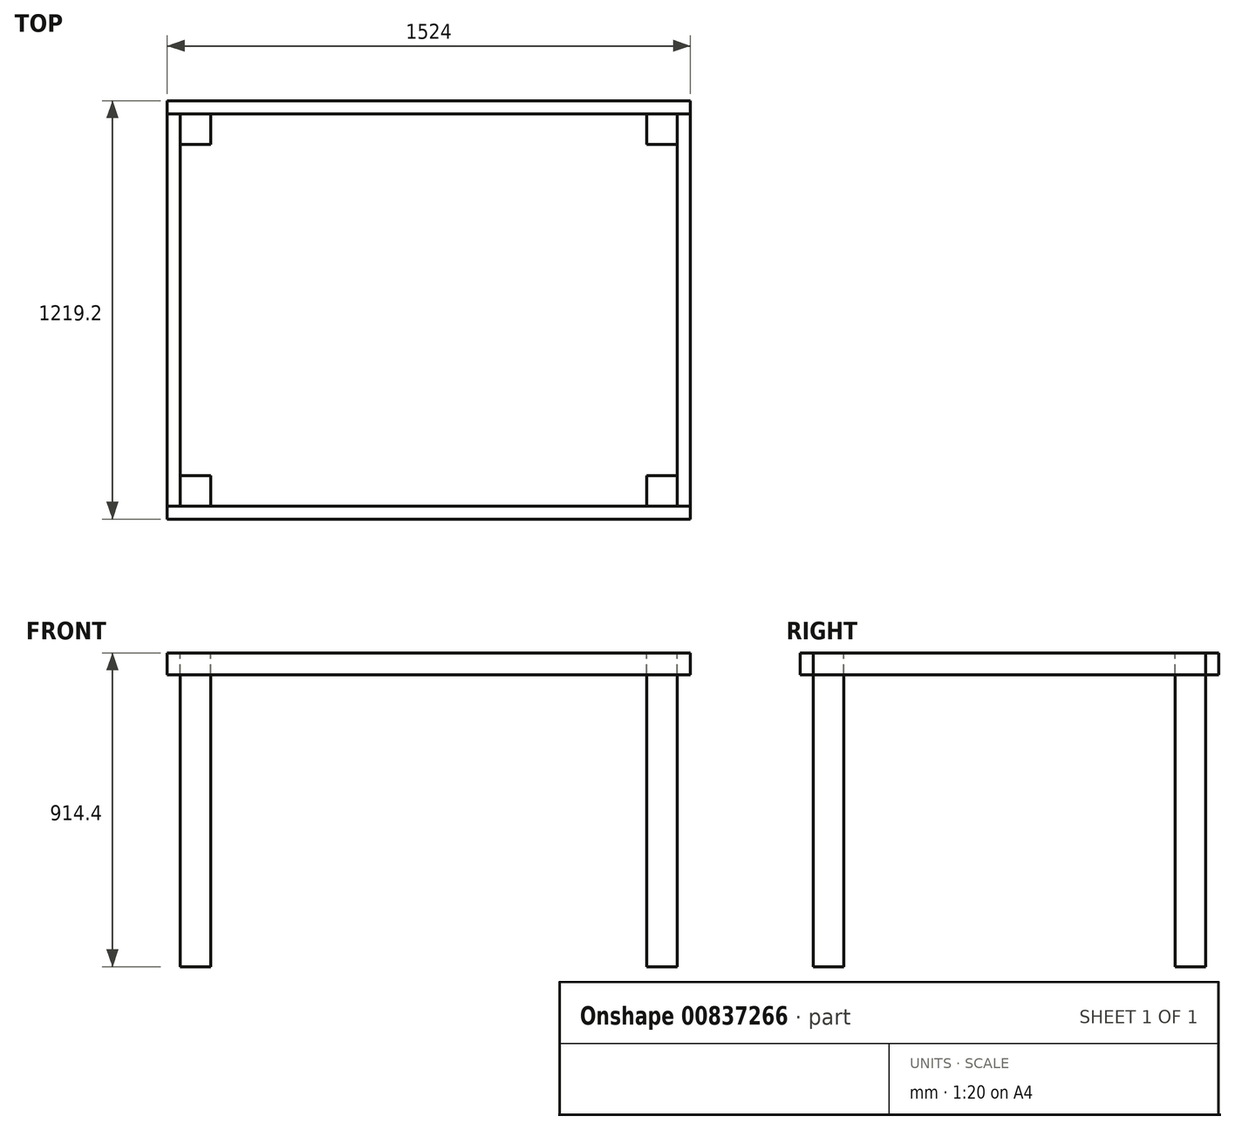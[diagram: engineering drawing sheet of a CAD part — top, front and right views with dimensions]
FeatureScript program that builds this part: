
annotation { "Feature Type Name" : "Feature", "Feature Type Description" : "" }
export const myFeature = defineFeature(function(context is Context, id is Id, definition is map)
    precondition{}
    {
        {
            var Q0;
            Q0=qCreatedBy(makeId("Top.planeOp"),FACE);
            var sketch = newSketch(context, id + "F0", { "sketchPlane" : qUnion([Q0])});
            skLineSegment(sketch, "E0.bottom", {"start": v(-762, -609.6) * mm, "end": v(762, -609.6) * mm});
            skLineSegment(sketch, "E0.top", {"start": v(-762, 609.6) * mm, "end": v(762, 609.6) * mm});
            skLineSegment(sketch, "E0.left", {"start": v(-762, -609.6) * mm, "end": v(-762, 609.6) * mm});
            skLineSegment(sketch, "E0.right", {"start": v(762, -609.6) * mm, "end": v(762, 609.6) * mm});
            skLineSegment(sketch, "E1", {"start": v(-762, -571.5) * mm, "end": v(762, -571.5) * mm});
            skLineSegment(sketch, "E2.MirrorCS", {"start": v(-762, 571.5) * mm, "end": v(762, 571.5) * mm});
            skLineSegment(sketch, "E3", {"start": v(-723.9, 571.5) * mm, "end": v(-723.9, -571.5) * mm});
            skLineSegment(sketch, "E4.MirrorCS", {"start": v(723.9, 571.5) * mm, "end": v(723.9, -571.5) * mm});
            skPoint(sketch, "E5.orphan", {"position": v(-723.9, -571.5) * mm});
            skPoint(sketch, "E6.orphan", {"position": v(-723.9, 571.5) * mm});
            skPoint(sketch, "E7.orphan", {"position": v(723.9, 571.5) * mm});
            skPoint(sketch, "E8.orphan", {"position": v(723.9, -571.5) * mm});
            skLineSegment(sketch, "E9.bottom", {"start": v(-723.9, -571.5) * mm, "end": v(-635, -571.5) * mm});
            skLineSegment(sketch, "E9.top", {"start": v(-723.9, -482.6) * mm, "end": v(-635, -482.6) * mm});
            skLineSegment(sketch, "E9.left", {"start": v(-723.9, -571.5) * mm, "end": v(-723.9, -482.6) * mm});
            skLineSegment(sketch, "E9.right", {"start": v(-635, -571.5) * mm, "end": v(-635, -482.6) * mm});
            skLineSegment(sketch, "E10.MirrorCS", {"start": v(-723.9, 482.6) * mm, "end": v(-635, 482.6) * mm});
            skLineSegment(sketch, "E11.MirrorCS", {"start": v(-635, 571.5) * mm, "end": v(-635, 482.6) * mm});
            skLineSegment(sketch, "E12.MirrorCS", {"start": v(635, 571.5) * mm, "end": v(635, 482.6) * mm});
            skLineSegment(sketch, "E13.MirrorCS", {"start": v(723.9, 482.6) * mm, "end": v(635, 482.6) * mm});
            skLineSegment(sketch, "E14.MirrorCS", {"start": v(723.9, -482.6) * mm, "end": v(635, -482.6) * mm});
            skLineSegment(sketch, "E15.MirrorCS", {"start": v(635, -571.5) * mm, "end": v(635, -482.6) * mm});
            skLineSegment(sketch, "E16", {"start": v(0, 127) * mm, "end": v(0, -127) * mm});
            skLineSegment(sketch, "E17", {"start": v(-127, 0) * mm, "end": v(127, 0) * mm});
            skLineSegment(sketch, "E18.MirrorCS", {"start": v(-635, 533.4) * mm, "end": v(635, 533.4) * mm});
            skLineSegment(sketch, "E19.MirrorCS", {"start": v(-635, -533.4) * mm, "end": v(635, -533.4) * mm});
            skLineSegment(sketch, "E20.MirrorCS", {"start": v(-685.8, -482.6) * mm, "end": v(-685.8, 482.6) * mm});
            skPoint(sketch, "E21.orphan", {"position": v(-762, -533.4) * mm});
            skPoint(sketch, "E22.orphan", {"position": v(-762, 533.4) * mm});
            skPoint(sketch, "E23.orphan", {"position": v(762, 533.4) * mm});
            skPoint(sketch, "E24.orphan", {"position": v(762, -533.4) * mm});
            skPoint(sketch, "E25.orphan", {"position": v(685.8, -609.6) * mm});
            skLineSegment(sketch, "E26.trimOffspring", {"start": v(685.8, -482.6) * mm, "end": v(685.8, 482.6) * mm});
            skPoint(sketch, "E27.orphan", {"position": v(-685.8, -609.6) * mm});
            skPoint(sketch, "E28.trimOffspring.end.orphan", {"position": v(-685.8, 609.6) * mm});
            skPoint(sketch, "E29.orphan", {"position": v(685.8, 609.6) * mm});
            skSolve(sketch);
        }
        {
            var Q0;
            {var subQ0=sQuery(id+"F0.wireOp",EDGE,"E9.top");Q0=makeQuery(id+"F0.imprint","IMPRINT",FACE,{"disambiguationData":[TD([[makeQuery(id+"F0.imprint","IMPRINT",EDGE,{"derivedFrom":subQ0}),-1.0]])]});}
            var Q1;
            {var subQ0=sQuery(id+"F0.wireOp",EDGE,"E9.bottom");Q1=makeQuery(id+"F0.imprint","IMPRINT",FACE,{"disambiguationData":[TD([[makeQuery(id+"F0.imprint","IMPRINT",EDGE,{"derivedFrom":subQ0}),1.0]])]});}
            extrude(context, id + "F1", {"entities" : qUnion([Q0, Q1]), "depth" : -914.4 * mm, "offsetDistance" : 25.4 * mm});
        }
        {
            var Q0;
            {var subQ0=sQuery(id+"F0.wireOp",EDGE,"E0.left");var subQ1=sQuery(id+"F0.wireOp",EDGE,"E0.bottom");var subQ2=makeQuery(id+"F0.imprint","INTERSECT",VERTEX,{"derivedFrom":[subQ1,subQ0]});Q0=makeQuery(id+"F0.imprint","IMPRINT",FACE,{"disambiguationData":[TD([[makeQuery(id+"F0.imprint","IMPRINT",EDGE,{"disambiguationData":[TD([[subQ2,-1.0]])],"derivedFrom":subQ1}),1.0]])]});}
            var Q1;
            {var subQ3=sQuery(id+"F0.wireOp",EDGE,"E9.bottom");Q1=makeQuery(id+"F0.imprint","IMPRINT",FACE,{"disambiguationData":[TD([[makeQuery(id+"F0.imprint","IMPRINT",EDGE,{"derivedFrom":subQ3}),-1.0]])]});}
            var Q2;
            {var subQ0=sQuery(id+"F0.wireOp",EDGE,"E0.right");var subQ1=sQuery(id+"F0.wireOp",EDGE,"E0.bottom");var subQ2=makeQuery(id+"F0.imprint","INTERSECT",VERTEX,{"derivedFrom":[subQ1,subQ0]});Q2=makeQuery(id+"F0.imprint","IMPRINT",FACE,{"disambiguationData":[TD([[makeQuery(id+"F0.imprint","IMPRINT",EDGE,{"disambiguationData":[TD([[subQ2,1.0]])],"derivedFrom":subQ1}),1.0]])]});}
            extrude(context, id + "F2", {"entities" : qUnion([Q0, Q1, Q2]), "depth" : -63.5 * mm, "offsetDistance" : 25.4 * mm});
        }
        {
            var Q0;
            {var subQ4=sQuery(id+"F0.wireOp",EDGE,"E1");var subQ5=sQuery(id+"F0.wireOp",EDGE,"E0.left");var subQ6=makeQuery(id+"F0.imprint","INTERSECT",VERTEX,{"derivedFrom":[subQ5,subQ4]});Q0=makeQuery(id+"F0.imprint","IMPRINT",FACE,{"disambiguationData":[TD([[makeQuery(id+"F0.imprint","IMPRINT",EDGE,{"disambiguationData":[TD([[subQ6,-1.0]])],"derivedFrom":subQ5}),-1.0]])]});}
            var Q1;
            {var subQ1=sQuery(id+"F0.wireOp",EDGE,"E0.right");var subQ7=makeQuery(id+"F0.imprint","IMPRINT",VERTEX,{"derivedFrom":subQ1});Q1=makeQuery(id+"F0.imprint","IMPRINT",FACE,{"disambiguationData":[TD([[makeQuery(id+"F0.imprint","IMPRINT",EDGE,{"disambiguationData":[TD([[subQ7,1.0]])],"derivedFrom":subQ1}),1.0]])]});}
            extrude(context, id + "F3", {"entities" : qUnion([Q0, Q1]), "depth" : -63.5 * mm, "offsetDistance" : 25.4 * mm});
        }
        {
            var Q0;
            Q0=makeQuery(id+"F1.opExtrude","SWEPT_BODY",BODY,{"disambiguationData":[OSD([sQuery(id+"F0.wireOp",EDGE,"E9.bottom"),sQuery(id+"F0.wireOp",EDGE,"E9.top"),sQuery(id+"F0.wireOp",EDGE,"E9.left"),sQuery(id+"F0.wireOp",EDGE,"E9.right")])]});
            var Q1;
            Q1=makeQuery(id+"F3.opExtrude","SWEPT_BODY",BODY,{"disambiguationData":[OSD([sQuery(id+"F0.wireOp",EDGE,"E0.left"),sQuery(id+"F0.wireOp",EDGE,"E1"),sQuery(id+"F0.wireOp",EDGE,"E2.MirrorCS"),sQuery(id+"F0.wireOp",EDGE,"E3"),sQuery(id+"F0.wireOp",EDGE,"E9.left")])]});
            var Q2;
            Q2=makeQuery(id+"FjySVfzRFTG0qzt_8.opExtrude","SWEPT_BODY",BODY,{"disambiguationData":[OSD([sQuery(id+"F6o8R0HqUV6JCXL_7.wireOp",EDGE,"svZ7ysUD-ZsJq-24mP-ykx9-nU1f8tRvwPk9.bottom"),sQuery(id+"F6o8R0HqUV6JCXL_7.wireOp",EDGE,"svZ7ysUD-ZsJq-24mP-ykx9-nU1f8tRvwPk9.top"),sQuery(id+"F6o8R0HqUV6JCXL_7.wireOp",EDGE,"svZ7ysUD-ZsJq-24mP-ykx9-nU1f8tRvwPk9.left"),sQuery(id+"F6o8R0HqUV6JCXL_7.wireOp",EDGE,"svZ7ysUD-ZsJq-24mP-ykx9-nU1f8tRvwPk9.right")])]});
            var Q3;
            Q3=qCreatedBy(makeId("Right.planeOp"),FACE);
            mirror(context, id + "F4", {"entities" : qUnion([Q0, Q1, Q2]), "mirrorPlane" : qUnion([Q3])});
        }
        {
            var Q0;
            Q0=makeQuery(id+"F1.opExtrude","SWEPT_BODY",BODY,{"disambiguationData":[OSD([sQuery(id+"F0.wireOp",EDGE,"E9.bottom"),sQuery(id+"F0.wireOp",EDGE,"E9.top"),sQuery(id+"F0.wireOp",EDGE,"E9.left"),sQuery(id+"F0.wireOp",EDGE,"E9.right")])]});
            var Q1;
            Q1=makeQuery(id+"F4.opPattern","COPY",BODY,{"derivedFrom":makeQuery(id+"F1.opExtrude","SWEPT_BODY",BODY,{"disambiguationData":[OSD([sQuery(id+"F0.wireOp",EDGE,"E9.bottom"),sQuery(id+"F0.wireOp",EDGE,"E9.top"),sQuery(id+"F0.wireOp",EDGE,"E9.left"),sQuery(id+"F0.wireOp",EDGE,"E9.right")])]}),"instanceName":"1"});
            var Q2;
            Q2=makeQuery(id+"F2.opExtrude","SWEPT_BODY",BODY,{"disambiguationData":[OSD([sQuery(id+"F0.wireOp",EDGE,"E0.bottom"),sQuery(id+"F0.wireOp",EDGE,"E0.left"),sQuery(id+"F0.wireOp",EDGE,"E0.right"),sQuery(id+"F0.wireOp",EDGE,"E1"),sQuery(id+"F0.wireOp",EDGE,"E9.bottom")])]});
            var Q3;
            Q3=makeQuery(id+"FLdhmSefsSLsmsZ_7.opExtrude","SWEPT_BODY",BODY,{"disambiguationData":[OSD([sQuery(id+"F6o8R0HqUV6JCXL_7.wireOp",EDGE,"o8AOivwl-ISV9-907b-gEv0-zonvCgLZ65xu.bottom"),sQuery(id+"F6o8R0HqUV6JCXL_7.wireOp",EDGE,"o8AOivwl-ISV9-907b-gEv0-zonvCgLZ65xu.top"),sQuery(id+"F6o8R0HqUV6JCXL_7.wireOp",EDGE,"o8AOivwl-ISV9-907b-gEv0-zonvCgLZ65xu.right"),sQuery(id+"F6o8R0HqUV6JCXL_7.wireOp",EDGE,"svZ7ysUD-ZsJq-24mP-ykx9-nU1f8tRvwPk9.left")])]});
            var Q4;
            Q4=qCreatedBy(makeId("Front.planeOp"),FACE);
            mirror(context, id + "F5", {"entities" : qUnion([Q0, Q1, Q2, Q3]), "mirrorPlane" : qUnion([Q4])});
        }
    });
